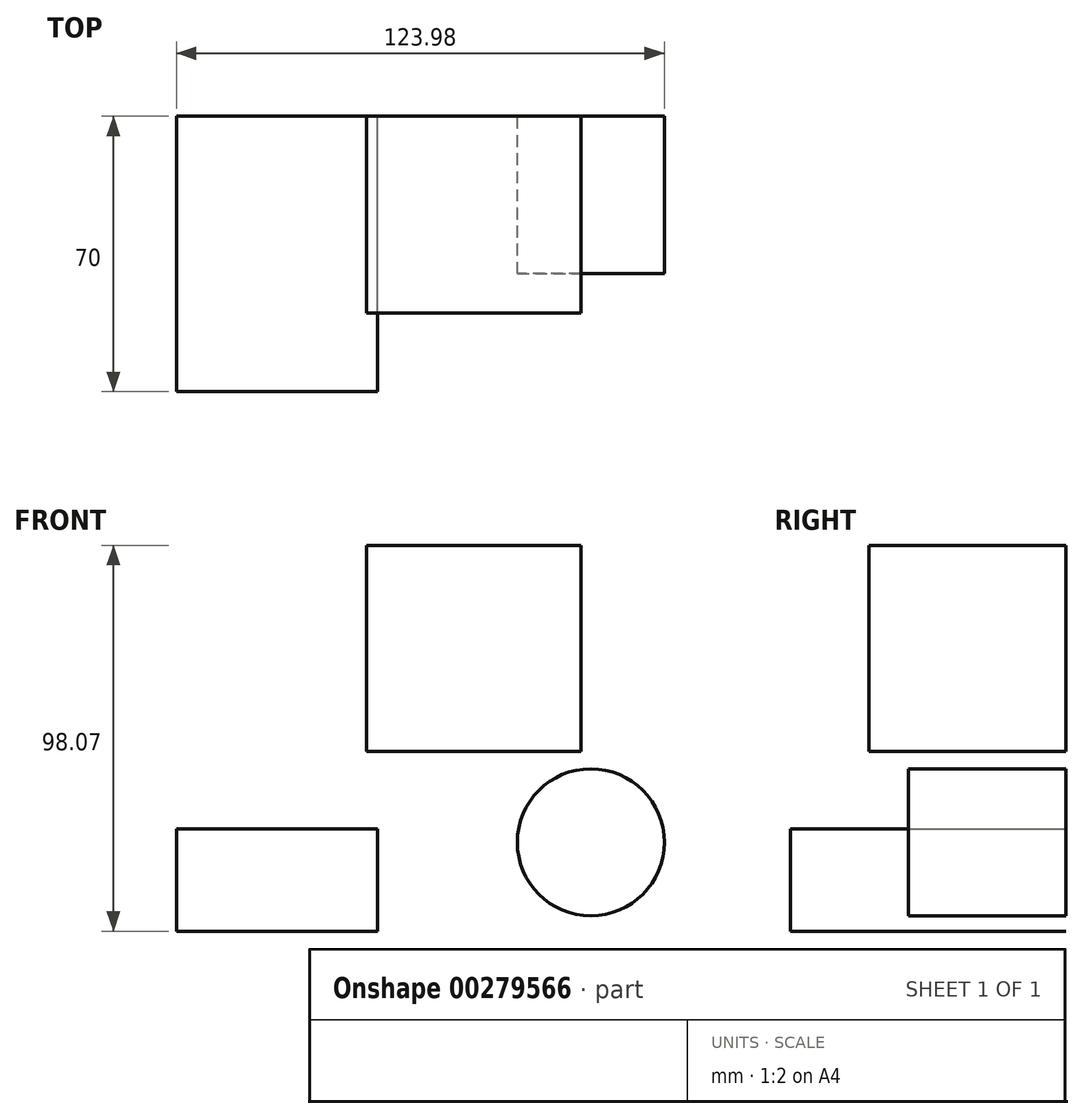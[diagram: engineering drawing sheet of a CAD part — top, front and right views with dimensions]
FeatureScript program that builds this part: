
annotation { "Feature Type Name" : "Feature", "Feature Type Description" : "" }
export const myFeature = defineFeature(function(context is Context, id is Id, definition is map)
    precondition{}
    {
        {
            var Q0;
            Q0=qCreatedBy(makeId("Front.planeOp"),FACE);
            var sketch = newSketch(context, id + "F0", { "sketchPlane" : qUnion([Q0])});
            skLineSegment(sketch, "E0.bottom", {"start": v(38.19, 54.35) * mm, "end": v(-16.27, 54.35) * mm});
            skLineSegment(sketch, "E0.top", {"start": v(38.19, 1.92) * mm, "end": v(-16.27, 1.92) * mm});
            skLineSegment(sketch, "E0.left", {"start": v(38.19, 54.35) * mm, "end": v(38.19, 1.92) * mm});
            skLineSegment(sketch, "E0.right", {"start": v(-16.27, 54.35) * mm, "end": v(-16.27, 1.92) * mm});
            skSolve(sketch);
        }
        {
            var Q0;
            Q0=makeQuery(id+"F0.imprint","IMPRINT",FACE,{"disambiguationData":[TD([[makeQuery(id+"F0.imprint","IMPRINT",EDGE,{"derivedFrom":sQuery(id+"F0.wireOp",EDGE,"E0.bottom")}),1.0]])]});
            extrude(context, id + "F1", {"entities" : qUnion([Q0]), "depth" : 50 * mm});
        }
        {
            var Q0;
            Q0=qCreatedBy(makeId("Front.planeOp"),FACE);
            var sketch = newSketch(context, id + "F2", { "sketchPlane" : qUnion([Q0])});
            skLineSegment(sketch, "E1.bottom", {"start": v(-13.56, -17.74) * mm, "end": v(-64.63, -17.74) * mm});
            skLineSegment(sketch, "E1.top", {"start": v(-13.56, -43.72) * mm, "end": v(-64.63, -43.72) * mm});
            skLineSegment(sketch, "E1.left", {"start": v(-13.56, -17.74) * mm, "end": v(-13.56, -43.72) * mm});
            skLineSegment(sketch, "E1.right", {"start": v(-64.63, -17.74) * mm, "end": v(-64.63, -43.72) * mm});
            skSolve(sketch);
        }
        {
            var Q0;
            Q0=makeQuery(id+"F2.imprint","IMPRINT",FACE,{"disambiguationData":[TD([[makeQuery(id+"F2.imprint","IMPRINT",EDGE,{"derivedFrom":sQuery(id+"F2.wireOp",EDGE,"E1.bottom")}),1.0]])]});
            extrude(context, id + "F3", {"entities" : qUnion([Q0]), "depth" : 70 * mm});
        }
        {
            var Q0;
            Q0=qCreatedBy(makeId("Front.planeOp"),FACE);
            var sketch = newSketch(context, id + "F4", { "sketchPlane" : qUnion([Q0])});
            skCircle(sketch, "E2", {"center": v(40.67, -21.13) * mm, "radius": 18.68 * mm});
            skSolve(sketch);
        }
        {
            var Q0;
            Q0=makeQuery(id+"F4.imprint","IMPRINT",FACE,{"disambiguationData":[TD([[makeQuery(id+"F4.imprint","IMPRINT",EDGE,{"derivedFrom":sQuery(id+"F4.wireOp",EDGE,"E2")}),1.0]])]});
            extrude(context, id + "F5", {"entities" : qUnion([Q0]), "depth" : 40 * mm});
        }
    });
